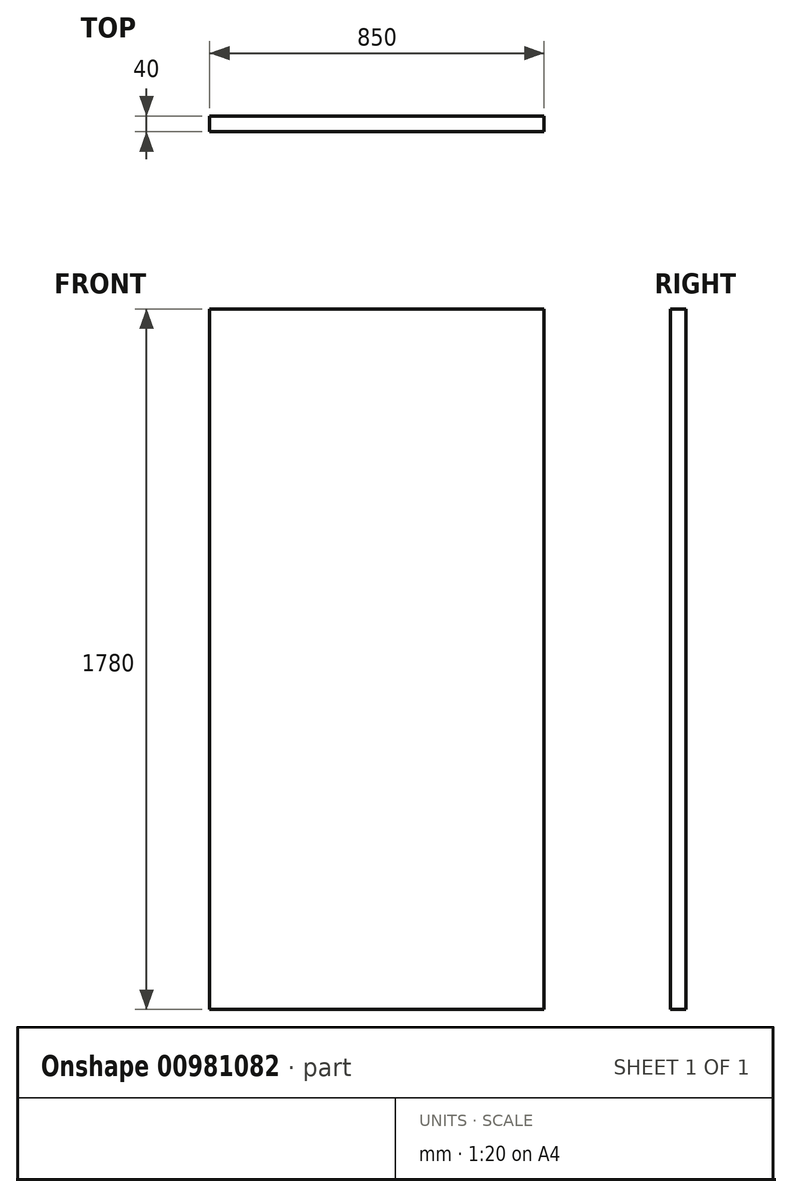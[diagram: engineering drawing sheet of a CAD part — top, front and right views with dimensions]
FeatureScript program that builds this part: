
annotation { "Feature Type Name" : "Feature", "Feature Type Description" : "" }
export const myFeature = defineFeature(function(context is Context, id is Id, definition is map)
    precondition{}
    {
        {
            var Q0;
            Q0=qCreatedBy(makeId("Front.planeOp"),FACE);
            var sketch = newSketch(context, id + "F0", { "sketchPlane" : qUnion([Q0])});
            skLineSegment(sketch, "E0", {"start": v(0, 0) * mm, "end": v(0, 95.43) * mm, "construction": true});
            skLineSegment(sketch, "E1.bottom", {"start": v(425, 0) * mm, "end": v(-425, 0) * mm});
            skLineSegment(sketch, "E1.top", {"start": v(425, 1780) * mm, "end": v(-425, 1780) * mm});
            skLineSegment(sketch, "E1.left", {"start": v(425, 0) * mm, "end": v(425, 1780) * mm});
            skLineSegment(sketch, "E1.right", {"start": v(-425, 0) * mm, "end": v(-425, 1780) * mm});
            skSolve(sketch);
        }
        {
            var Q0;
            Q0 = qSketchRegion(id + "F0", true);
            extrude(context, id + "F1", {"entities" : qUnion([Q0]), "endBound" : BoundingType.SYMMETRIC, "depth" : 40 * mm, "offsetDistance" : 25 * mm});
        }
    });
